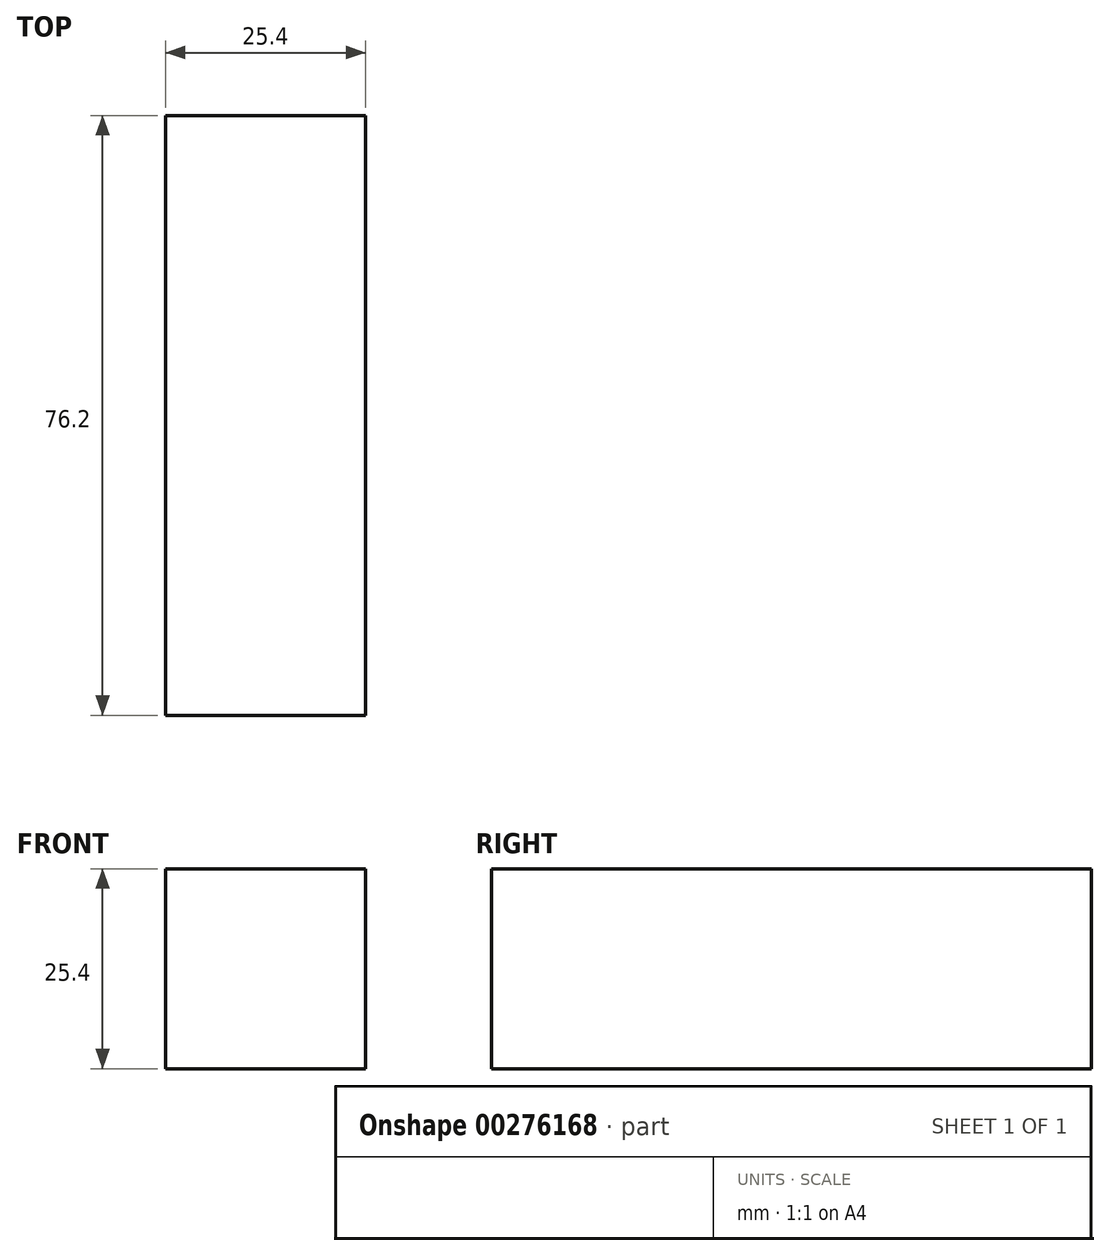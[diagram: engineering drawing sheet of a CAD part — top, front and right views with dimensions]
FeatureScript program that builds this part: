
annotation { "Feature Type Name" : "Feature", "Feature Type Description" : "" }
export const myFeature = defineFeature(function(context is Context, id is Id, definition is map)
    precondition{}
    {
        {
            var Q0;
            Q0=qCreatedBy(makeId("Front.planeOp"),FACE);
            var sketch = newSketch(context, id + "F0", { "sketchPlane" : qUnion([Q0])});
            skLineSegment(sketch, "E0.bottom", {"start": v(45.45, 0) * mm, "end": v(20.05, 0) * mm});
            skLineSegment(sketch, "E0.top", {"start": v(45.45, 25.4) * mm, "end": v(20.05, 25.4) * mm});
            skLineSegment(sketch, "E0.left", {"start": v(45.45, 0) * mm, "end": v(45.45, 25.4) * mm});
            skLineSegment(sketch, "E0.right", {"start": v(20.05, 0) * mm, "end": v(20.05, 25.4) * mm});
            skSolve(sketch);
        }
        {
            var Q0;
            Q0 = qSketchRegion(id + "F0", true);
            extrude(context, id + "F1", {"entities" : qUnion([Q0]), "depth" : 76.2 * mm});
        }
    });
